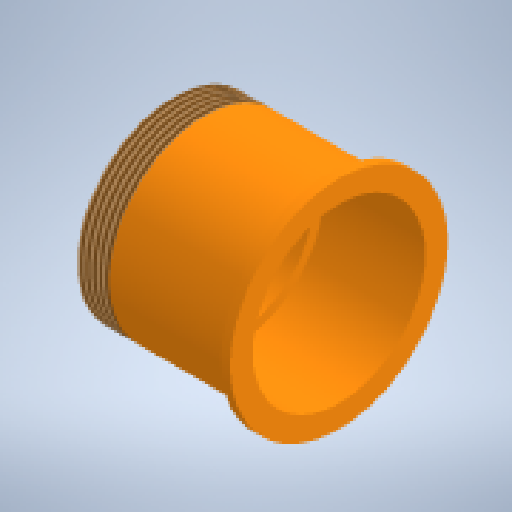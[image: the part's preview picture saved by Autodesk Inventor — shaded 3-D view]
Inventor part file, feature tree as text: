
AUTODESK INVENTOR PART (.ipt)
format: ipt  version: 2023 (Build 270158000, 158)  size: 190,976 bytes
history: native  units: mm
features: revolve x1, thread x1
ambient origin geometry x8: Origin, YZ Plane, XZ Plane, XY Plane, X Axis, Y Axis, Z Axis, Center Point
bodies: Solid1 (feature_tree)
feature tree (2):
  revolve  "Revolution1"  [1 undecoded]
  thread  "Thread1"  [1 undecoded]
note: 2 required parameter values undecoded (feature->parameter linkage not recoverable at this tier; creation-order binding heuristic only, values carry confidence <= 0.55)